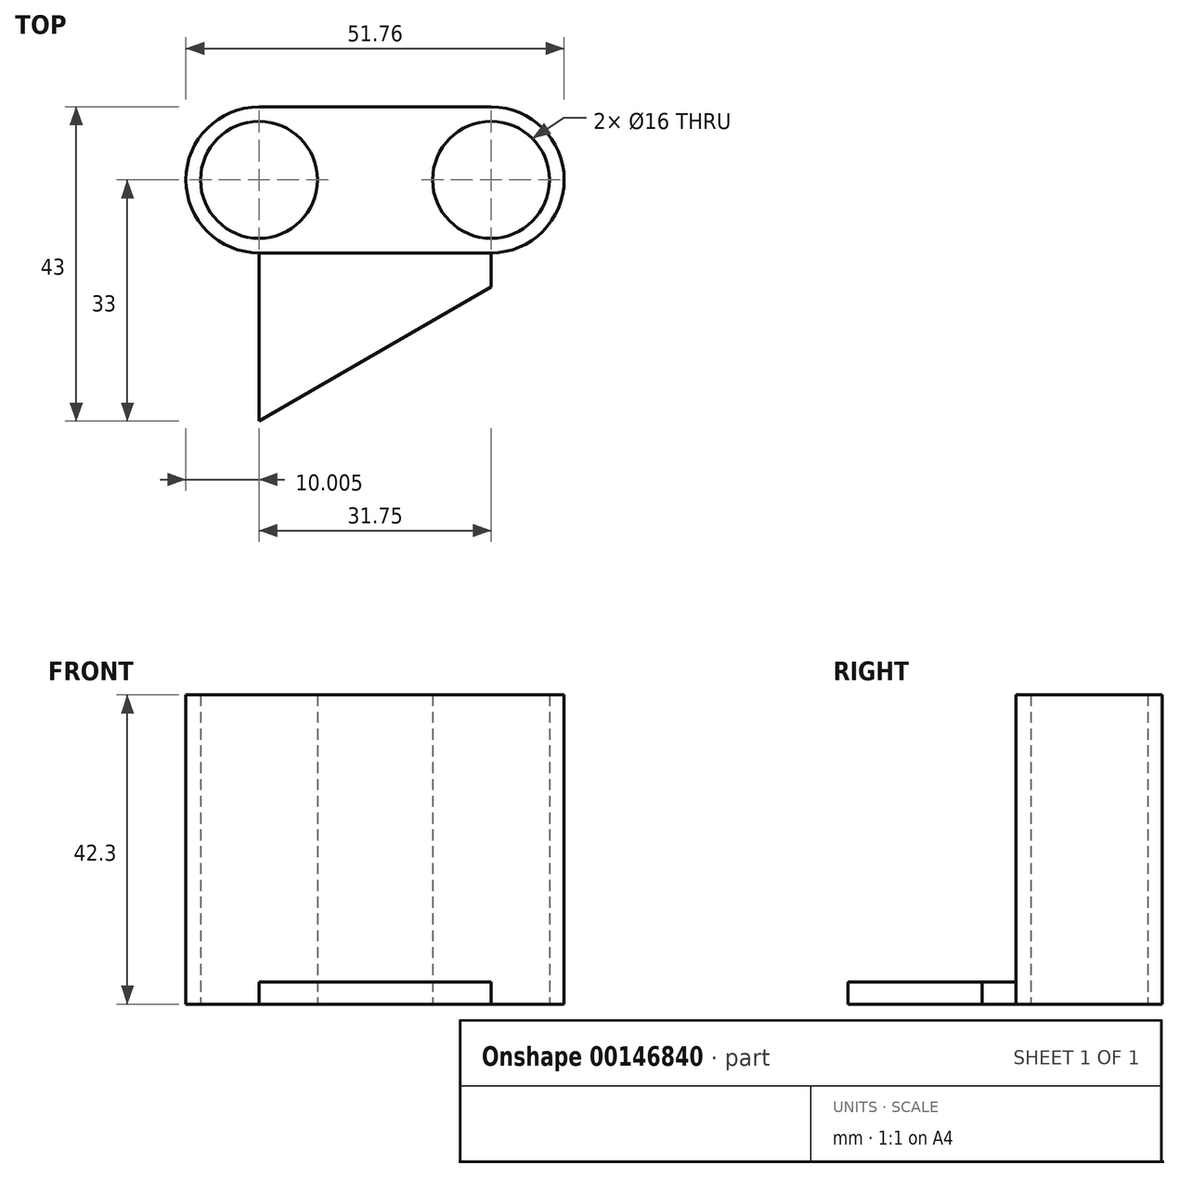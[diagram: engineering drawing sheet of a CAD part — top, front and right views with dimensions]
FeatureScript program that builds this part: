
annotation { "Feature Type Name" : "Feature", "Feature Type Description" : "" }
export const myFeature = defineFeature(function(context is Context, id is Id, definition is map)
    precondition{}
    {
        {
            var Q0;
            Q0=qCreatedBy(makeId("Top.planeOp"),FACE);
            var sketch = newSketch(context, id + "F0", { "sketchPlane" : qUnion([Q0])});
            skCircle(sketch, "E0", {"center": v(-15.88, 0) * mm, "radius": 8 * mm});
            skCircle(sketch, "E1", {"center": v(15.88, 0) * mm, "radius": 8 * mm});
            skArc(sketch, "E2", {"start": v(15.88, -10) * mm, "mid": v(25.88, 0) * mm, "end": v(15.88, 10) * mm});
            skArc(sketch, "E3", {"start": v(-15.88, 10) * mm, "mid": v(-25.88, 0) * mm, "end": v(-15.88, -10) * mm});
            skLineSegment(sketch, "E4", {"start": v(-15.88, 0) * mm, "end": v(15.88, 0) * mm, "construction": true});
            skLineSegment(sketch, "E5", {"start": v(-15.88, 10) * mm, "end": v(15.88, 10) * mm});
            skLineSegment(sketch, "E6", {"start": v(-15.88, -10) * mm, "end": v(15.88, -10) * mm});
            skSolve(sketch);
        }
        {
            var Q0;
            Q0=qSketchRegion(id+"F0",true);
            extrude(context, id + "F1", {"entities" : qUnion([Q0]), "depth" : 42.3 * mm});
        }
        {
            var Q0;
            Q0=qCreatedBy(makeId("Top.planeOp"),FACE);
            var sketch = newSketch(context, id + "F2", { "sketchPlane" : qUnion([Q0])});
            skLineSegment(sketch, "E7.0", {"start": v(-15.88, -10) * mm, "end": v(15.88, -10) * mm, "construction": true});
            skLineSegment(sketch, "E8.bottom", {"start": v(15.88, -10) * mm, "end": v(-15.88, -10) * mm});
            skLineSegment(sketch, "E8.top", {"start": v(15.88, -33) * mm, "end": v(-15.87, -33) * mm});
            skLineSegment(sketch, "E8.left", {"start": v(15.88, -10) * mm, "end": v(15.88, -33) * mm});
            skLineSegment(sketch, "E8.right", {"start": v(-15.88, -10) * mm, "end": v(-15.87, -33) * mm});
            skSolve(sketch);
        }
        {
            var Q0;
            Q0=qSketchRegion(id+"F2",true);
            extrude(context, id + "F3", {"entities" : qUnion([Q0]), "operationType" : NewBodyOperationType.ADD, "depth" : 3 * mm});
        }
        {
            var Q0;
            Q0=makeQuery(id+"F3.boolean.opBoolean","MERGE",FACE,{"derivedFrom":[makeQuery(id+"F1.opExtrude","CAP_FACE",FACE,{"disambiguationData":[OSD([sQuery(id+"F0.wireOp",EDGE,"E0"),sQuery(id+"F0.wireOp",EDGE,"E1"),sQuery(id+"F0.wireOp",EDGE,"E2"),sQuery(id+"F0.wireOp",EDGE,"E3"),sQuery(id+"F0.wireOp",EDGE,"E5"),sQuery(id+"F0.wireOp",EDGE,"E6")])],"isStart":true}),makeQuery(id+"F3.opExtrude","CAP_FACE",FACE,{"disambiguationData":[OSD([sQuery(id+"F2.wireOp",EDGE,"E8.bottom"),sQuery(id+"F2.wireOp",EDGE,"E8.top"),sQuery(id+"F2.wireOp",EDGE,"E8.left"),sQuery(id+"F2.wireOp",EDGE,"E8.right")])],"isStart":true})]});
            var sketch = newSketch(context, id + "F4", { "sketchPlane" : qUnion([Q0])});
            skLineSegment(sketch, "E9", {"start": v(-15.87, 33) * mm, "end": v(15.87, 14.67) * mm});
            skLineSegment(sketch, "E10", {"start": v(15.87, 14.67) * mm, "end": v(15.88, 33) * mm});
            skLineSegment(sketch, "E11", {"start": v(15.88, 33) * mm, "end": v(-15.87, 33) * mm});
            skSolve(sketch);
        }
        {
            var Q0;
            Q0 = qSketchRegion(id + "F4", true);
            extrude(context, id + "F5", {"entities" : qUnion([Q0]), "operationType" : NewBodyOperationType.REMOVE, "oppositeDirection" : true, "depth" : 25 * mm});
        }
    });
